# Revit family: Base_Cabinets-Teknion-RHBD_Base_Cabinet_with_Drawers_and_Doors-R2018
name_source: partatom
category: Furniture
revit_build: Autodesk Revit 2018 (Build: 20170223_1515(x64)
units: mm (PartAtom-declared; Revit-internal decimal feet)

## family parameters
Always vertical = Yes
Cut with Voids When Loaded = No
OmniClass Number = 23.40.20.00
OmniClass Title = General Furniture and Specialties
Room Calculation Point = No
Shared = Yes
Work Plane-Based = No

## types (8) — shared parameters
Assembly Code = E2020200
Manufacturer = Teknion
Manufacturer Fax = 416.661.4586
Part Number = RHBD
Product Documentation Link = https://www.teknion.com
Product Line = Modular Cabinets
Product Page URL = https://www.teknion.com
Series = Modular Cabinets
Sustainability Data = https://www.teknion.com
URL = www.teknion.com
Unit Weight URL = http://www.teknion.com
Warranty = http://www.teknion.com

## per-type parameters (varying)
| type | Depth | Description | Drawer Height Offset | Height | Model | One Drawer | Shelf Height Offset | Two Drawer Cut Depth | Two Drawers |
| One Drawer, 24" Depth, 33" Height | 24 " | Base Cabinet with Drawer(s) and Door(s), One Drawer, 24" Depth, 33" Height | 7.013 " | 32.5 " | RHBDO24__33_ | Yes | 13.884 " | 0.5 " | No |
| One Drawer, 29" Depth, 33" Height | 29 " | Base Cabinet with Drawer(s) and Door(s), One Drawer, 29" Depth, 33" Height | 7.013 " | 32.5 " | RHBDO29__33_ | Yes | 13.884 " | 0.5 " | No |
| One Drawer, 29" Depth, 35" Height | 29 " | Base Cabinet with Drawer(s) and Door(s), One Drawer, 29" Depth, 35" Height | 7.638 " | 35 " | RHBDO29__35_ | Yes | 15.134 " | 0.5 " | No |
| One Drawer, 24" Depth, 35" Height | 24 " | Base Cabinet with Drawer(s) and Door(s), One Drawer, 24" Depth, 35" Height | 7.638 " | 35 " | RHBDO24__35_ | Yes | 15.134 " | 0.5 " | No |
| Two Drawers, 24" Depth, 33" Height | 24 " | Base Cabinet with Drawer(s) and Door(s), Two Drawers, 24" Depth, 33" Height | 7.013 " | 32.5 " | RHBDT24__33_ | No | 13.884 " | 7.701 " | Yes |
| Two Drawers, 24" Depth, 35" Height | 24 " | Base Cabinet with Drawer(s) and Door(s), Two Drawers, 24" Depth, 35" Height | 7.638 " | 35 " | RHBDT24__35_ | No | 15.134 " | 7.701 " | Yes |
| Two Drawers, 29" Depth, 33" Height | 29 " | Base Cabinet with Drawer(s) and Door(s), Two Drawers, 29" Depth, 33" Height | 7.013 " | 32.5 " | RHBDT29__33_ | No | 13.884 " | 7.701 " | Yes |
| Two Drawers, 29" Depth, 35" Height | 29 " | Base Cabinet with Drawer(s) and Door(s), Two Drawers, 29" Depth, 35" Height | 7.638 " | 35 " | RHBDT29__35_ | No | 15.134 " | 7.701 " | Yes |

## geometry (parser evidence)
native form markers: Sweep x2
no freeform markers — native parametric forms only
